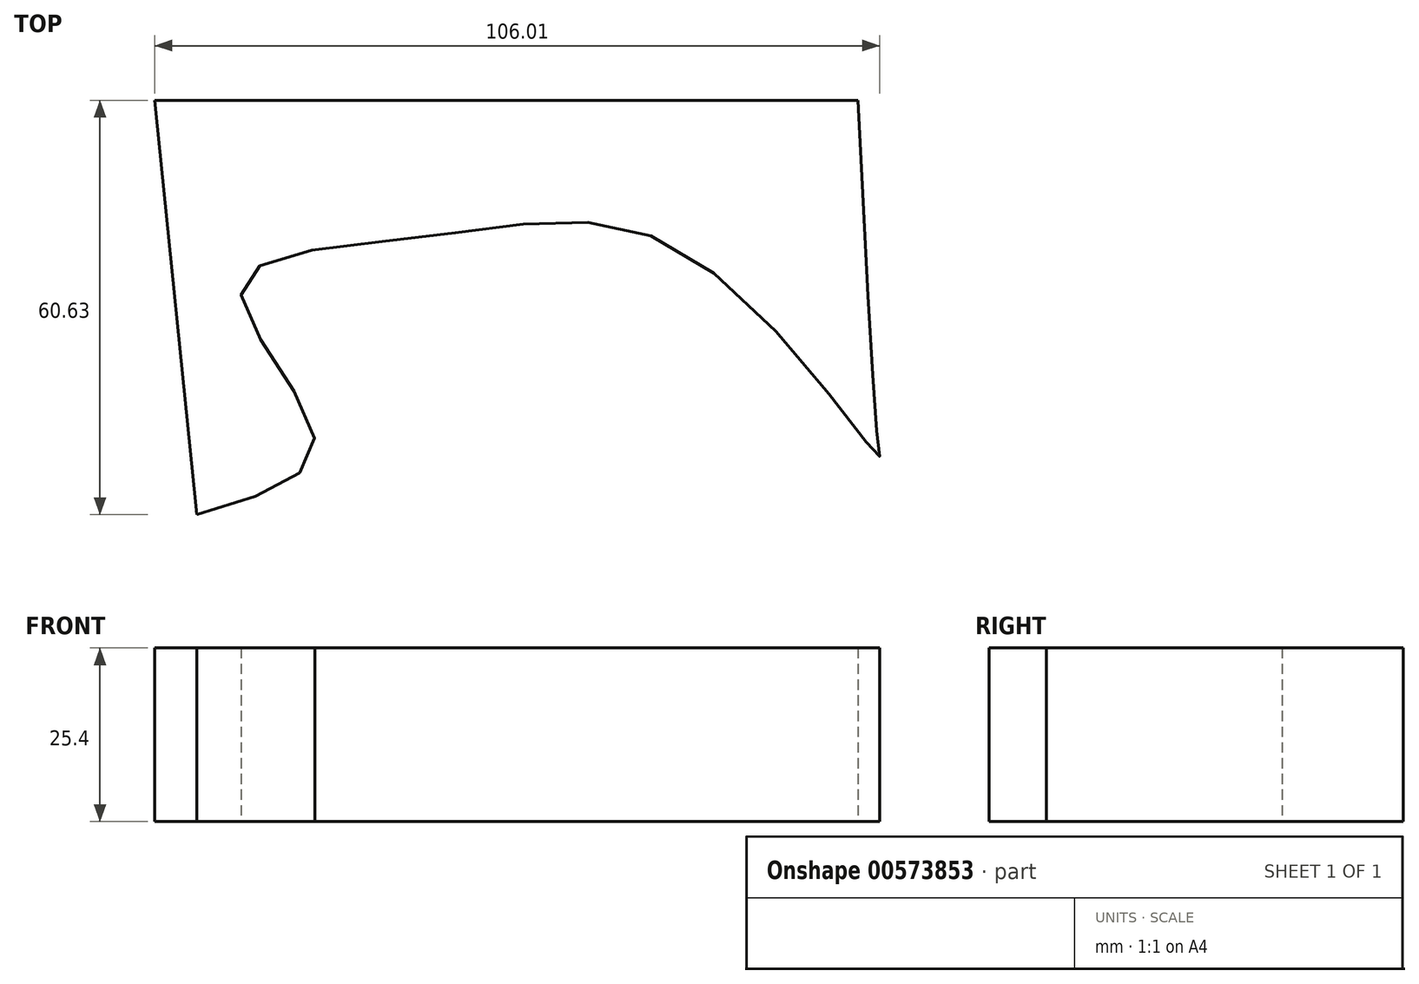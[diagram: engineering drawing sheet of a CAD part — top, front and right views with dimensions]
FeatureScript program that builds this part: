
annotation { "Feature Type Name" : "Feature", "Feature Type Description" : "" }
export const myFeature = defineFeature(function(context is Context, id is Id, definition is map)
    precondition{}
    {
        {
            var Q0;
            Q0=qCreatedBy(makeId("Top.planeOp"),FACE);
            var sketch = newSketch(context, id + "F0", { "sketchPlane" : qUnion([Q0])});
            skLineSegment(sketch, "E0", {"start": v(-44.13, 36.26) * mm, "end": v(58.71, 36.26) * mm});
            skFitSpline(sketch, "E1", {"points": [v(-38, -24.37) * mm, v(-20.72, -13.62) * mm, v(-31.47, 8.63) * mm, v(-4.22, 16.3) * mm, v(34.54, 13.24) * mm, v(61.78, -15.93) * mm, v(61.78, -15.16) * mm, v(58.71, 36.26) * mm], "startDerivative": vector(206.03, 58.45) * mm, "endDerivative": vector(-17.65, 346.12) * mm});
            skLineSegment(sketch, "E2", {"start": v(-44.13, 36.26) * mm, "end": v(-38, -24.37) * mm});
            skSolve(sketch);
        }
        {
            var Q0;
            Q0 = qSketchRegion(id + "F0", true);
            extrude(context, id + "F1", {"entities" : qUnion([Q0]), "depth" : 25.4 * mm, "offsetDistance" : 25.4 * mm});
        }
    });
